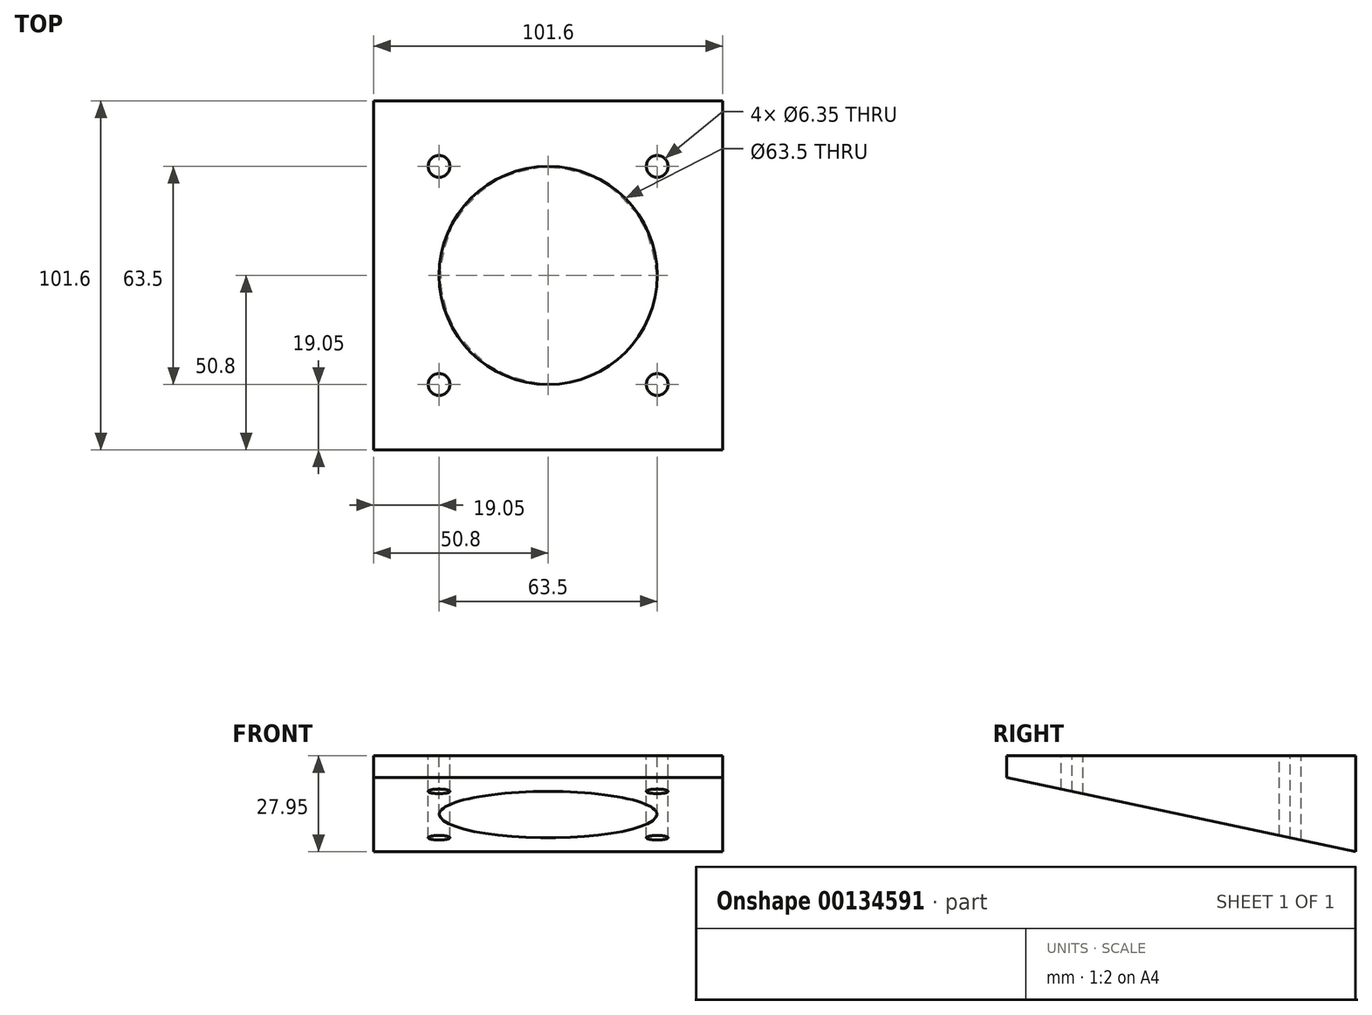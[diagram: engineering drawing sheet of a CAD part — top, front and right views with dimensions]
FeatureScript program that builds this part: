
annotation { "Feature Type Name" : "Feature", "Feature Type Description" : "" }
export const myFeature = defineFeature(function(context is Context, id is Id, definition is map)
    precondition{}
    {
        {
            var Q0;
            Q0=qCreatedBy(makeId("Top.planeOp"),FACE);
            var sketch = newSketch(context, id + "F0", { "sketchPlane" : qUnion([Q0])});
            skLineSegment(sketch, "E0.bottom", {"start": v(-50.8, 50.8) * mm, "end": v(50.8, 50.8) * mm});
            skLineSegment(sketch, "E0.top", {"start": v(-50.8, -50.8) * mm, "end": v(50.8, -50.8) * mm});
            skLineSegment(sketch, "E0.left", {"start": v(-50.8, 50.8) * mm, "end": v(-50.8, -50.8) * mm});
            skLineSegment(sketch, "E0.right", {"start": v(50.8, 50.8) * mm, "end": v(50.8, -50.8) * mm});
            skCircle(sketch, "E1", {"center": v(0, 0) * mm, "radius": 31.75 * mm});
            skCircle(sketch, "E2", {"center": v(-31.75, 31.75) * mm, "radius": 3.18 * mm});
            skCircle(sketch, "E3.0.1.0", {"center": v(-31.75, -31.75) * mm, "radius": 3.18 * mm});
            skCircle(sketch, "E3.1.0.0", {"center": v(31.75, 31.75) * mm, "radius": 3.18 * mm});
            skCircle(sketch, "E3.1.1.0", {"center": v(31.75, -31.75) * mm, "radius": 3.18 * mm});
            skLineSegment(sketch, "E3.direction1", {"start": v(-31.75, 31.75) * mm, "end": v(31.75, 31.75) * mm, "construction": true});
            skLineSegment(sketch, "E3.direction2", {"start": v(-31.75, 31.75) * mm, "end": v(-31.75, -31.75) * mm, "construction": true});
            skSolve(sketch);
        }
        {
            var Q0;
            Q0=qCreatedBy(makeId("Right.planeOp"),FACE);
            var sketch = newSketch(context, id + "F1", { "sketchPlane" : qUnion([Q0])});
            skLineSegment(sketch, "E4", {"start": v(-50.8, 0) * mm, "end": v(-50.8, -6.35) * mm});
            skLineSegment(sketch, "E5", {"start": v(-50.8, -6.35) * mm, "end": v(50.8, -27.95) * mm});
            skLineSegment(sketch, "E6", {"start": v(50.8, -27.95) * mm, "end": v(50.8, 0) * mm});
            skLineSegment(sketch, "E7", {"start": v(-50.8, 0) * mm, "end": v(50.8, 0) * mm});
            skSolve(sketch);
        }
        {
            var Q0;
            Q0 = qSketchRegion(id + "F1", true);
            extrude(context, id + "F2", {"entities" : qUnion([Q0]), "depth" : 50.8 * mm, "hasSecondDirection" : true, "secondDirectionOppositeDirection" : true, "secondDirectionDepth" : 50.8 * mm});
        }
        {
            var Q0;
            Q0=sQuery(id+"F0.wireOp",VERTEX,"E3.direction2.start");
            var Q1;
            Q1=sQuery(id+"F0.wireOp",VERTEX,"E3.direction1.end");
            var Q2;
            Q2=sQuery(id+"F0.wireOp",VERTEX,"E3.1.1.0.center");
            var Q3;
            Q3=sQuery(id+"F0.wireOp",VERTEX,"E3.direction2.end");
            var Q4;
            Q4=makeQuery(id+"F2.opExtrude","SWEPT_BODY",BODY,{"disambiguationData":[OSD([sQuery(id+"F1.wireOp",EDGE,"E4"),sQuery(id+"F1.wireOp",EDGE,"E5"),sQuery(id+"F1.wireOp",EDGE,"E6"),sQuery(id+"F1.wireOp",EDGE,"E7")])]});
            hole(context, id + "F3", {"style" : HoleStyle.SIMPLE, "endStyle" : HoleEndStyle.THROUGH, "holeDiameter" : 6.35 * mm, "locations" : qUnion([Q0, Q1, Q2, Q3]), "scope" : qUnion([Q4]), "isTappedThrough" : true});
        }
        {
            var Q0;
            Q0=makeQuery(id+"F2.opExtrude","SWEPT_FACE",FACE,{"disambiguationData":[OSD([sQuery(id+"F1.wireOp",EDGE,"E7")])]});
            var sketch = newSketch(context, id + "F4", { "sketchPlane" : qUnion([Q0])});
            skCircle(sketch, "E8", {"center": v(0, 0) * mm, "radius": 31.75 * mm, "construction": true});
            skSolve(sketch);
        }
        {
            var Q0;
            Q0=sQuery(id+"F4.wireOp",VERTEX,"E8.center");
            var Q1;
            Q1=makeQuery(id+"F2.opExtrude","SWEPT_BODY",BODY,{"disambiguationData":[OSD([sQuery(id+"F1.wireOp",EDGE,"E4"),sQuery(id+"F1.wireOp",EDGE,"E5"),sQuery(id+"F1.wireOp",EDGE,"E6"),sQuery(id+"F1.wireOp",EDGE,"E7")])]});
            hole(context, id + "F5", {"style" : HoleStyle.SIMPLE, "endStyle" : HoleEndStyle.THROUGH, "holeDiameter" : 63.5 * mm, "locations" : qUnion([Q0]), "scope" : qUnion([Q1]), "isTappedThrough" : true});
        }
    });
